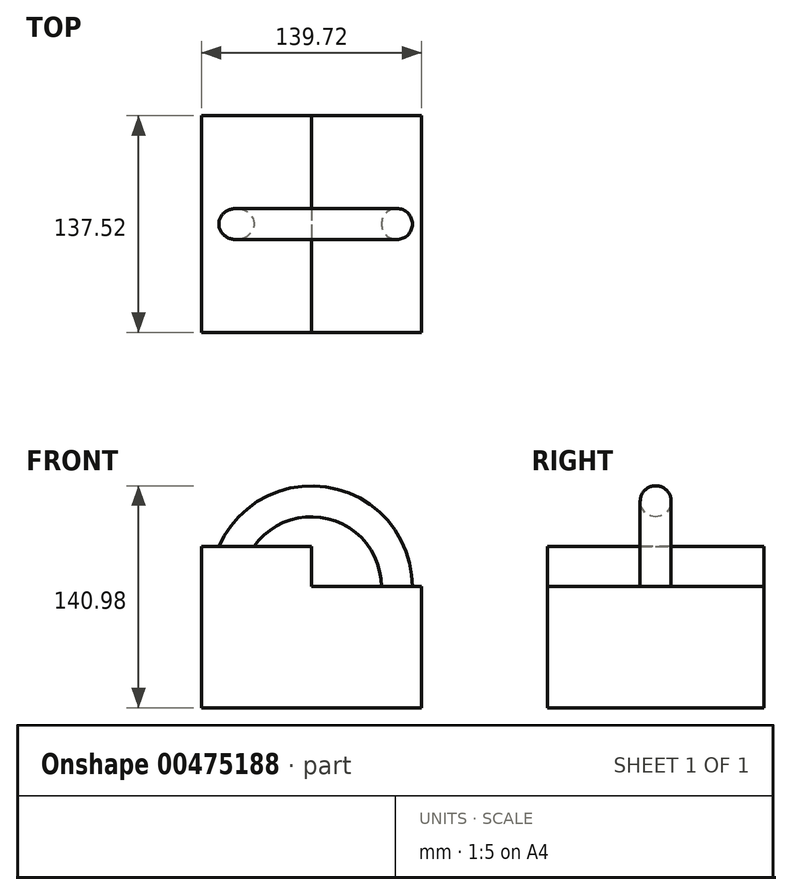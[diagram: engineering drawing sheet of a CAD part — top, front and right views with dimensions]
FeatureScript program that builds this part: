
annotation { "Feature Type Name" : "Feature", "Feature Type Description" : "" }
export const myFeature = defineFeature(function(context is Context, id is Id, definition is map)
    precondition{}
    {
        {
            var Q0;
            Q0=qCreatedBy(makeId("Top.planeOp"),FACE);
            var sketch = newSketch(context, id + "F0", { "sketchPlane" : qUnion([Q0])});
            skLineSegment(sketch, "E0.bottom", {"start": v(69.86, -68.76) * mm, "end": v(-69.86, -68.76) * mm});
            skLineSegment(sketch, "E0.top", {"start": v(69.86, 68.76) * mm, "end": v(-69.86, 68.76) * mm});
            skLineSegment(sketch, "E0.left", {"start": v(69.86, -68.76) * mm, "end": v(69.86, 68.76) * mm});
            skLineSegment(sketch, "E0.right", {"start": v(-69.86, -68.76) * mm, "end": v(-69.86, 68.76) * mm});
            skPoint(sketch, "E0.middle", {"position": v(0, 0) * mm});
            skLineSegment(sketch, "E1", {"start": v(0, 68.76) * mm, "end": v(0, -68.76) * mm});
            skSolve(sketch);
        }
        {
            var Q0;
            Q0=qCreatedBy(makeId("Top.planeOp"),FACE);
            var sketch = newSketch(context, id + "F1", { "sketchPlane" : qUnion([Q0])});
            skCircle(sketch, "E2", {"center": v(54.26, 0) * mm, "radius": 9.82 * mm});
            skSolve(sketch);
        }
        {
            var Q0;
            {var subQ0=sQuery(id+"F0.wireOp",EDGE,"E0.right");Q0=makeQuery(id+"F0.imprint","IMPRINT",FACE,{"disambiguationData":[TD([[makeQuery(id+"F0.imprint","IMPRINT",EDGE,{"derivedFrom":subQ0}),-1.0]])]});}
            var Q1;
            {var subQ0=sQuery(id+"F0.wireOp",EDGE,"E0.left");Q1=makeQuery(id+"F0.imprint","IMPRINT",FACE,{"disambiguationData":[TD([[makeQuery(id+"F0.imprint","IMPRINT",EDGE,{"derivedFrom":subQ0}),1.0]])]});}
            extrude(context, id + "F2", {"entities" : qUnion([Q0, Q1]), "oppositeDirection" : true, "depth" : 76.9 * mm});
        }
        {
            var Q0;
            Q0=makeQuery(id+"F1.imprint","IMPRINT",FACE,{"disambiguationData":[TD([[makeQuery(id+"F1.imprint","IMPRINT",EDGE,{"derivedFrom":sQuery(id+"F1.wireOp",EDGE,"E2")}),1.0]])]});
            var Q1;
            Q1=sQuery(id+"F0.wireOp",EDGE,"E1");
            revolve(context, id + "F3", {"operationType" : NewBodyOperationType.ADD, "entities" : qUnion([Q0]), "axis" : qUnion([Q1]), "revolveType" : RevolveType.FULL});
        }
        {
            var Q0;
            {var subQ0=sQuery(id+"F0.wireOp",EDGE,"E0.right");Q0=makeQuery(id+"F0.imprint","IMPRINT",FACE,{"disambiguationData":[TD([[makeQuery(id+"F0.imprint","IMPRINT",EDGE,{"derivedFrom":subQ0}),-1.0]])]});}
            extrude(context, id + "F4", {"entities" : qUnion([Q0]), "operationType" : NewBodyOperationType.ADD, "depth" : 25.4 * mm});
        }
        {
            var Q0;
            Q0=makeQuery(id+"F4.opExtrude","CAP_FACE",FACE,{"disambiguationData":[OSD([sQuery(id+"F0.wireOp",EDGE,"E0.bottom"),sQuery(id+"F0.wireOp",EDGE,"E0.top"),sQuery(id+"F0.wireOp",EDGE,"E0.right"),sQuery(id+"F0.wireOp",EDGE,"E1")])],"isStart":false});
            extrude(context, id + "F5", {"entities" : qUnion([Q0]), "operationType" : NewBodyOperationType.ADD, "oppositeDirection" : true, "depth" : 25.4 * mm});
        }
        {
            var Q0;
            Q0=makeQuery(id+"F4.opExtrude","CAP_FACE",FACE,{"disambiguationData":[OSD([sQuery(id+"F0.wireOp",EDGE,"E0.bottom"),sQuery(id+"F0.wireOp",EDGE,"E0.top"),sQuery(id+"F0.wireOp",EDGE,"E0.right"),sQuery(id+"F0.wireOp",EDGE,"E1")])],"isStart":false});
            extrude(context, id + "F6", {"entities" : qUnion([Q0]), "operationType" : NewBodyOperationType.ADD, "oppositeDirection" : true, "depth" : 25.4 * mm});
        }
    });
